# Revit family: RN 81164 Optipress-Aquaplus-Valvola di ritegno EA
name_source: partatom
category: Rohrzubehör
units: mm (PartAtom-declared; Revit-internal decimal feet)

## family parameters
Arbeitsebenenbasiert = Nein
Beim Laden mit Abzugskörper schneiden = Nein
Bemaßung runder Anschluss = Durchmesser verwenden
Gemeinsam genutzt = Nein
Immer vertikal = Ja
Teiletyp = Ventil - Zerlegung in

## types (5) — shared parameters
1.010.00.2 Number of the part of the guideline = 17
1.010.00.3 Issue date (month) of the guideline = 201601
1.010.00.4 Manufacturer name = R. Nussbaum AG
1.010.00.5 Revision date of the file = 20190528
1.100.00.3 Sort number for display sequence = 4
1.100.00.4 Product designation = Rubinetti di sicurezza e a conduttura circolare
1.960/3L.00.8 Link (URL) = https://www.nussbaum.ch
17.700.00.4 valve assembly type = 6
17.700.00.7 maximum operating temperature TB [°C] = 90
17.700.00.8 maximum operating pressure(working pressure) ps [1.0 · 105 Pa] = 16
Connector Visibility = Nein
EnclosingSpace Visibility = Nein

## per-type parameters (varying)
- DN 20: 1.800.00.3 BS number=0040250000000000000000000000020070000000000000000100000000; 1.810.00.3 Manufacturer’s reference number=81164.24; 1.810.00.4 DATANORM number=81164.24; 1.810.00.5 StLB number=614.854; 1.810.00.6 GTIN number=7612945737403; 17.700.00.30 product description=81164.24, Optipress-Aquaplus-Valvola di ritegno EA, con filetto femmina, DN=20, R; 17.700.00.5 nominal size DN=20; 17.700.00.6 kvs-value [m3/h]=10.8; CONNECTOR0_DIAMETER_dZ_0r=20 mm; CONNECTOR0_dZ_00=70 mm; CONNECTOR0_dZ_01=46 mm; CONNECTOR0_ref_dZ=46 mm; CONNECTOR1_DIAMETER_dZ_0r=20 mm; CONNECTOR1_dZ_00=32 mm; CONNECTOR1_dZ_01=56 mm; CONNECTOR1_ref_dZ=32 mm; CONNECTOR2_DIAMETER_dX_0r=20 mm; CONNECTOR2_dX_00=29 mm  [stored 0.0951444 ft]; CONNECTOR2_dX_01=44 mm; CONNECTOR2_ref_dX=29 mm  [stored 0.0951444 ft]; CONNECTOR2_ref_dZ=3 mm  [stored 0.00984252 ft]; R. Nussbaum AG 81164.24 it Visibility=Ja; R. Nussbaum AG 81164.25 it Visibility=Nein; R. Nussbaum AG 81164.26 it Visibility=Nein; R. Nussbaum AG 81164.27 it Visibility=Nein; R. Nussbaum AG 81164.30 it Visibility=Nein
- DN 25: 1.800.00.3 BS number=0040250000000000000000000000020070000000000000000200000000; 1.810.00.3 Manufacturer’s reference number=81164.25; 1.810.00.4 DATANORM number=81164.25; 1.810.00.5 StLB number=614.855; 1.810.00.6 GTIN number=7612945738110; 17.700.00.30 product description=81164.25, Optipress-Aquaplus-Valvola di ritegno EA, con filetto femmina, DN=25, R; 17.700.00.5 nominal size DN=25; 17.700.00.6 kvs-value [m3/h]=16.8; CONNECTOR0_DIAMETER_dZ_0r=25 mm  [stored 0.082021 ft]; CONNECTOR0_dZ_00=74 mm; CONNECTOR0_dZ_01=50 mm; CONNECTOR0_ref_dZ=50 mm; CONNECTOR1_DIAMETER_dZ_0r=25 mm  [stored 0.082021 ft]; CONNECTOR1_dZ_00=37 mm; CONNECTOR1_dZ_01=61 mm; CONNECTOR1_ref_dZ=37 mm; CONNECTOR2_DIAMETER_dX_0r=20 mm; CONNECTOR2_dX_00=34 mm; CONNECTOR2_dX_01=49 mm; CONNECTOR2_ref_dX=34 mm; CONNECTOR2_ref_dZ=4 mm  [stored 0.0131234 ft]; R. Nussbaum AG 81164.24 it Visibility=Nein; R. Nussbaum AG 81164.25 it Visibility=Ja; R. Nussbaum AG 81164.26 it Visibility=Nein; R. Nussbaum AG 81164.27 it Visibility=Nein; R. Nussbaum AG 81164.30 it Visibility=Nein
- DN 32: 1.800.00.3 BS number=0040250000000000000000000000020070000000000000000300000000; 1.810.00.3 Manufacturer’s reference number=81164.26; 1.810.00.4 DATANORM number=81164.26; 1.810.00.5 StLB number=614.856; 1.810.00.6 GTIN number=7612945735423; 17.700.00.30 product description=81164.26, Optipress-Aquaplus-Valvola di ritegno EA, con filetto femmina, DN=32, R; 17.700.00.5 nominal size DN=32; 17.700.00.6 kvs-value [m3/h]=31.2; CONNECTOR0_DIAMETER_dZ_0r=32 mm; CONNECTOR0_dZ_00=85 mm; CONNECTOR0_dZ_01=59 mm; CONNECTOR0_ref_dZ=59 mm; CONNECTOR1_DIAMETER_dZ_0r=32 mm; CONNECTOR1_dZ_00=44 mm; CONNECTOR1_dZ_01=70 mm; CONNECTOR1_ref_dZ=44 mm; CONNECTOR2_DIAMETER_dX_0r=20 mm; CONNECTOR2_dX_00=39 mm; CONNECTOR2_dX_01=54 mm; CONNECTOR2_ref_dX=39 mm; CONNECTOR2_ref_dZ=3 mm  [stored 0.00984252 ft]; R. Nussbaum AG 81164.24 it Visibility=Nein; R. Nussbaum AG 81164.25 it Visibility=Nein; R. Nussbaum AG 81164.26 it Visibility=Ja; R. Nussbaum AG 81164.27 it Visibility=Nein; R. Nussbaum AG 81164.30 it Visibility=Nein
- DN 40: 1.800.00.3 BS number=0040250000000000000000000000020070000000000000000400000000; 1.810.00.3 Manufacturer’s reference number=81164.27; 1.810.00.4 DATANORM number=81164.27; 1.810.00.5 StLB number=614.857; 1.810.00.6 GTIN number=7612945733825; 17.700.00.30 product description=81164.27, Optipress-Aquaplus-Valvola di ritegno EA, con filetto femmina, DN=40, R; 17.700.00.5 nominal size DN=40; 17.700.00.6 kvs-value [m3/h]=45; CONNECTOR0_DIAMETER_dZ_0r=40 mm; CONNECTOR0_dZ_00=100 mm  [stored 0.328084 ft]; CONNECTOR0_dZ_01=64 mm; CONNECTOR0_ref_dZ=64 mm; CONNECTOR1_DIAMETER_dZ_0r=40 mm; CONNECTOR1_dZ_00=49 mm; CONNECTOR1_dZ_01=85 mm; CONNECTOR1_ref_dZ=49 mm; CONNECTOR2_DIAMETER_dX_0r=25 mm  [stored 0.082021 ft]; CONNECTOR2_dX_00=27 mm  [stored 0.0885827 ft]; CONNECTOR2_dX_01=44 mm; CONNECTOR2_ref_dX=27 mm  [stored 0.0885827 ft]; CONNECTOR2_ref_dZ=4 mm  [stored 0.0131234 ft]; R. Nussbaum AG 81164.24 it Visibility=Nein; R. Nussbaum AG 81164.25 it Visibility=Nein; R. Nussbaum AG 81164.26 it Visibility=Nein; R. Nussbaum AG 81164.27 it Visibility=Ja; R. Nussbaum AG 81164.30 it Visibility=Nein
- DN 32 1: 1.800.00.3 BS number=0040250000000000000000000000020070000000000000000500000000; 1.810.00.3 Manufacturer’s reference number=81164.30; 1.810.00.4 DATANORM number=81164.30; 1.810.00.6 GTIN number=7612945735430; 17.700.00.30 product description=81164.30, Optipress-Aquaplus-Valvola di ritegno EA, con filetto femmina, DN=32, R; 17.700.00.5 nominal size DN=32; 17.700.00.6 kvs-value [m3/h]=31.2; CONNECTOR0_DIAMETER_dZ_0r=32 mm; CONNECTOR0_dZ_00=84 mm; CONNECTOR0_dZ_01=58 mm; CONNECTOR0_ref_dZ=58 mm; CONNECTOR1_DIAMETER_dZ_0r=32 mm; CONNECTOR1_dZ_00=45 mm; CONNECTOR1_dZ_01=71 mm; CONNECTOR1_ref_dZ=45 mm; CONNECTOR2_DIAMETER_dX_0r=20 mm; CONNECTOR2_dX_00=29 mm  [stored 0.0951444 ft]; CONNECTOR2_dX_01=44 mm; CONNECTOR2_ref_dX=29 mm  [stored 0.0951444 ft]; CONNECTOR2_ref_dZ=3 mm  [stored 0.00984252 ft]; R. Nussbaum AG 81164.24 it Visibility=Nein; R. Nussbaum AG 81164.25 it Visibility=Nein; R. Nussbaum AG 81164.26 it Visibility=Nein; R. Nussbaum AG 81164.27 it Visibility=Nein; R. Nussbaum AG 81164.30 it Visibility=Ja

note: [stored X ft] marks values corroborated as IEEE doubles in the binary element streams (Revit-internal decimal feet)

## geometry (parser evidence)
native form markers: Sweep x3
no freeform markers — native parametric forms only
